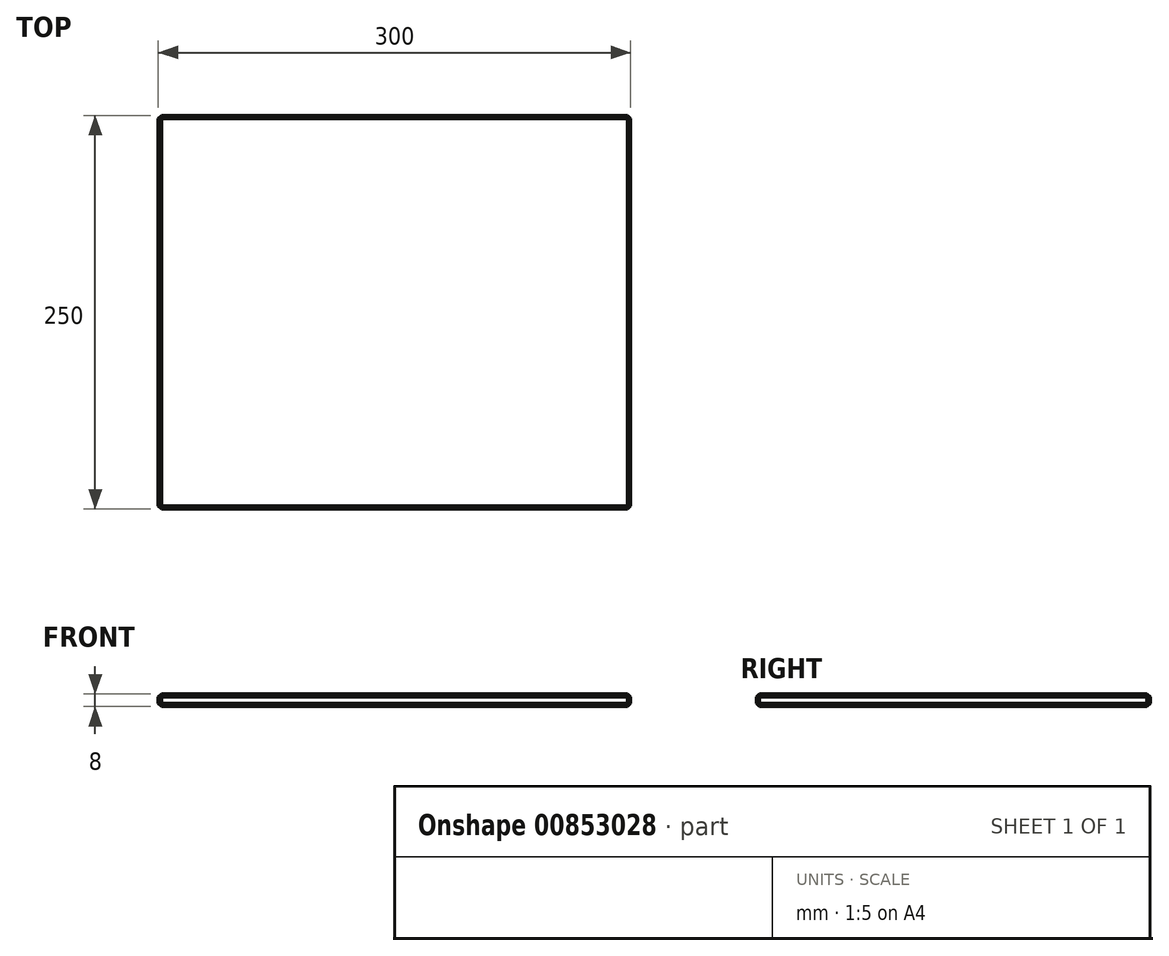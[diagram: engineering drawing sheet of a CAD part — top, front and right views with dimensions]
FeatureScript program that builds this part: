
annotation { "Feature Type Name" : "Feature", "Feature Type Description" : "" }
export const myFeature = defineFeature(function(context is Context, id is Id, definition is map)
    precondition{}
    {
        {
            var Q0;
            Q0=qCreatedBy(makeId("Top.planeOp"),FACE);
            var sketch = newSketch(context, id + "F0", { "sketchPlane" : qUnion([Q0])});
            skLineSegment(sketch, "E0.bottom", {"start": v(150, -125) * mm, "end": v(-150, -125) * mm});
            skLineSegment(sketch, "E0.top", {"start": v(150, 125) * mm, "end": v(-150, 125) * mm});
            skLineSegment(sketch, "E0.left", {"start": v(150, -125) * mm, "end": v(150, 125) * mm});
            skLineSegment(sketch, "E0.right", {"start": v(-150, -125) * mm, "end": v(-150, 125) * mm});
            skPoint(sketch, "E0.middle", {"position": v(0, 0) * mm});
            skSolve(sketch);
        }
        {
            var Q0;
            Q0 = qSketchRegion(id + "F0", true);
            extrude(context, id + "F1", {"entities" : qUnion([Q0]), "depth" : 8 * mm, "offsetDistance" : 25 * mm});
        }
        {
            var Q0;
            Q0=makeQuery(id+"F1.opExtrude","SWEPT_FACE",FACE,{"disambiguationData":[OSD([sQuery(id+"F0.wireOp",EDGE,"E0.bottom")])]});
            var Q1;
            Q1=makeQuery(id+"F1.opExtrude","SWEPT_FACE",FACE,{"disambiguationData":[OSD([sQuery(id+"F0.wireOp",EDGE,"E0.left")])]});
            var Q2;
            Q2=makeQuery(id+"F1.opExtrude","SWEPT_FACE",FACE,{"disambiguationData":[OSD([sQuery(id+"F0.wireOp",EDGE,"E0.top")])]});
            var Q3;
            Q3=makeQuery(id+"F1.opExtrude","SWEPT_FACE",FACE,{"disambiguationData":[OSD([sQuery(id+"F0.wireOp",EDGE,"E0.right")])]});
            chamfer(context, id + "F2", {"entities" : qUnion([Q0, Q1, Q2, Q3]), "width" : 2 * mm, "tangentPropagation" : true});
        }
    });
